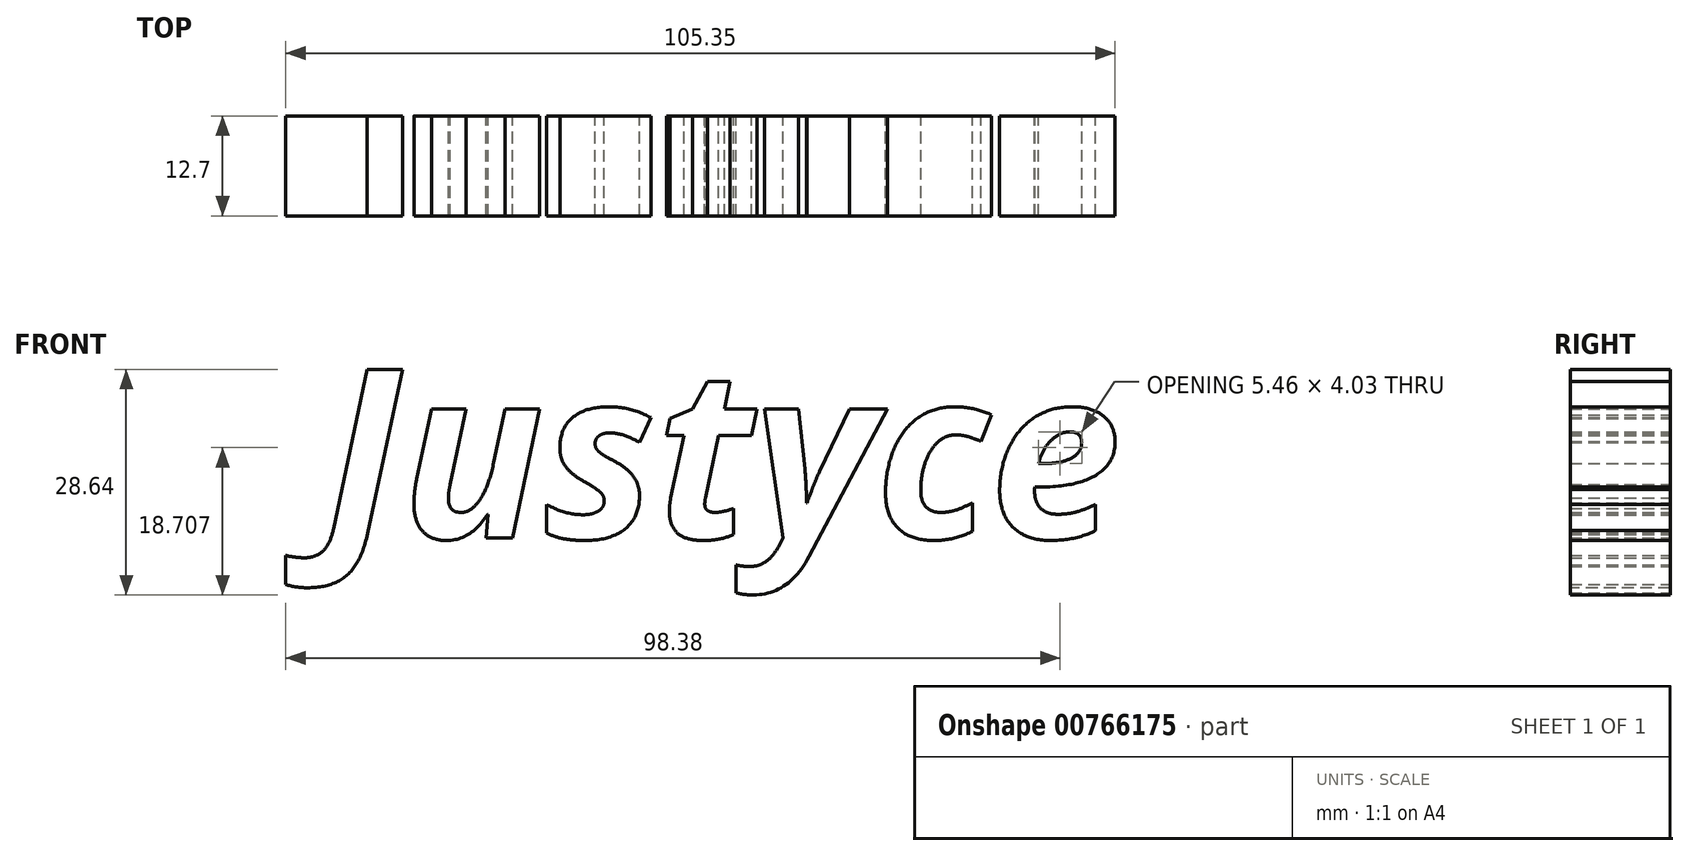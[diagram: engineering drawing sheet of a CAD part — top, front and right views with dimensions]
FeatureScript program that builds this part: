
annotation { "Feature Type Name" : "Feature", "Feature Type Description" : "" }
export const myFeature = defineFeature(function(context is Context, id is Id, definition is map)
    precondition{}
    {
        {
            var Q0;
            Q0=qCreatedBy(makeId("Front.planeOp"),FACE);
            var sketch = newSketch(context, id + "F0", { "sketchPlane" : qUnion([Q0])});
            skText(sketch, "E0", { "text": "Justyce", "fontName": "OpenSans-BoldItalic.ttf"});
            const initialGuessF0  = {"E0": [-0.06494, 0.00408, 1, 0, 0.02161]};
            skSetInitialGuess(sketch, initialGuessF0);
            skSolve(sketch);
        }
        {
            var Q0;
            Q0 = qSketchRegion(id + "F0", true);
            extrude(context, id + "F1", {"entities" : qUnion([Q0]), "depth" : 12.7 * mm, "offsetDistance" : 25.4 * mm});
        }
    });
